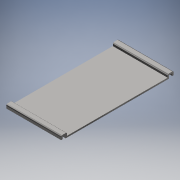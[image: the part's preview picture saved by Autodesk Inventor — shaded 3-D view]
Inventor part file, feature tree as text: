
AUTODESK INVENTOR PART (.ipt)
format: ipt  version: 2018 (Build 220112000, 112)  size: 128,512 bytes
history: native  units: in
note: dims shown in document units (in); Inventor stores cm internally (conversion verified against a paired STEP export)
features: extrude x1, fillet x1, sketch x1
ambient origin geometry x8: Origin, YZ Plane, XZ Plane, XY Plane, X Axis, Y Axis, Z Axis, Center Point
bodies: Solid1 (feature_tree)
feature tree (3):
  extrude  "Extrusion1"  Depth=74.0in
  fillet  "Fillet1"  Radius=2.5in
  sketch  "Sketch1"  dims[d4=1.0in d5=74.0in d7=2.5in d8=36.0in d9=0.0in d10=1.0in d11=2.0in d12=2.0in d13=2.0in d14=3.0in d15=1.0in d16=1.0in d17=1.0in]
